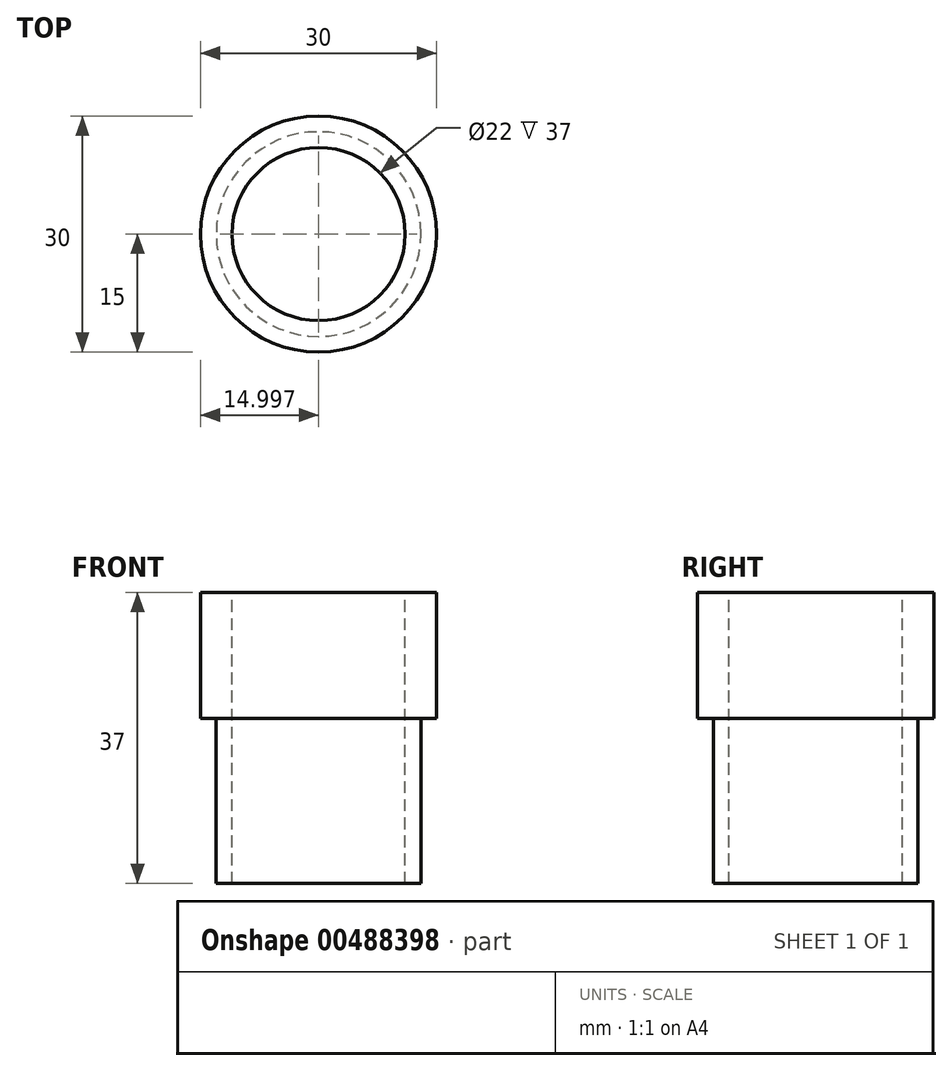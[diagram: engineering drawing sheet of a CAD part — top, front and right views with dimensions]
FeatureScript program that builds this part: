
annotation { "Feature Type Name" : "Feature", "Feature Type Description" : "" }
export const myFeature = defineFeature(function(context is Context, id is Id, definition is map)
    precondition{}
    {
        {
            var Q0;
            Q0=qCreatedBy(makeId("Front.planeOp"),FACE);
            var sketch = newSketch(context, id + "F0", { "sketchPlane" : qUnion([Q0])});
            skLineSegment(sketch, "E0.bottom", {"start": v(-23.97, 17.2) * mm, "end": v(-21.97, 17.2) * mm});
            skLineSegment(sketch, "E0.top", {"start": v(-23.97, -3.8) * mm, "end": v(-21.97, -3.8) * mm});
            skLineSegment(sketch, "E0.left", {"start": v(-23.97, 17.2) * mm, "end": v(-23.97, -3.8) * mm});
            skLineSegment(sketch, "E0.right", {"start": v(-21.97, 17.2) * mm, "end": v(-21.97, -3.8) * mm});
            skLineSegment(sketch, "E1.bottom", {"start": v(-21.97, 17.2) * mm, "end": v(-25.97, 17.2) * mm});
            skLineSegment(sketch, "E1.top", {"start": v(-21.97, 33.2) * mm, "end": v(-25.97, 33.2) * mm});
            skLineSegment(sketch, "E1.left", {"start": v(-21.97, 17.2) * mm, "end": v(-21.97, 33.2) * mm});
            skLineSegment(sketch, "E1.right", {"start": v(-25.97, 17.2) * mm, "end": v(-25.97, 33.2) * mm});
            skSolve(sketch);
        }
        {
            var Q0;
            Q0=qCreatedBy(makeId("Front.planeOp"),FACE);
            var sketch = newSketch(context, id + "F1", { "sketchPlane" : qUnion([Q0])});
            skLineSegment(sketch, "E2", {"start": v(-10.97, 35.35) * mm, "end": v(-10.97, -9.43) * mm});
            skSolve(sketch);
        }
        {
            var Q0;
            Q0 = qSketchRegion(id + "F1", true);
            var Q1;
            Q1=makeQuery(id+"F0.imprint","IMPRINT",FACE,{"disambiguationData":[TD([[makeQuery(id+"F0.imprint","IMPRINT",EDGE,{"derivedFrom":sQuery(id+"F0.wireOp",EDGE,"E1.top")}),1.0]])]});
            var Q2;
            Q2=makeQuery(id+"F0.imprint","IMPRINT",FACE,{"disambiguationData":[TD([[makeQuery(id+"F0.imprint","IMPRINT",EDGE,{"derivedFrom":sQuery(id+"F0.wireOp",EDGE,"E0.top")}),1.0]])]});
            var Q3;
            Q3=sQuery(id+"F1.wireOp",EDGE,"E2");
            revolve(context, id + "F2", {"surfaceOperationType" : NewSurfaceOperationType.NEW, "entities" : qUnion([Q0, Q1, Q2]), "axis" : qUnion([Q3]), "revolveType" : RevolveType.FULL});
        }
    });
